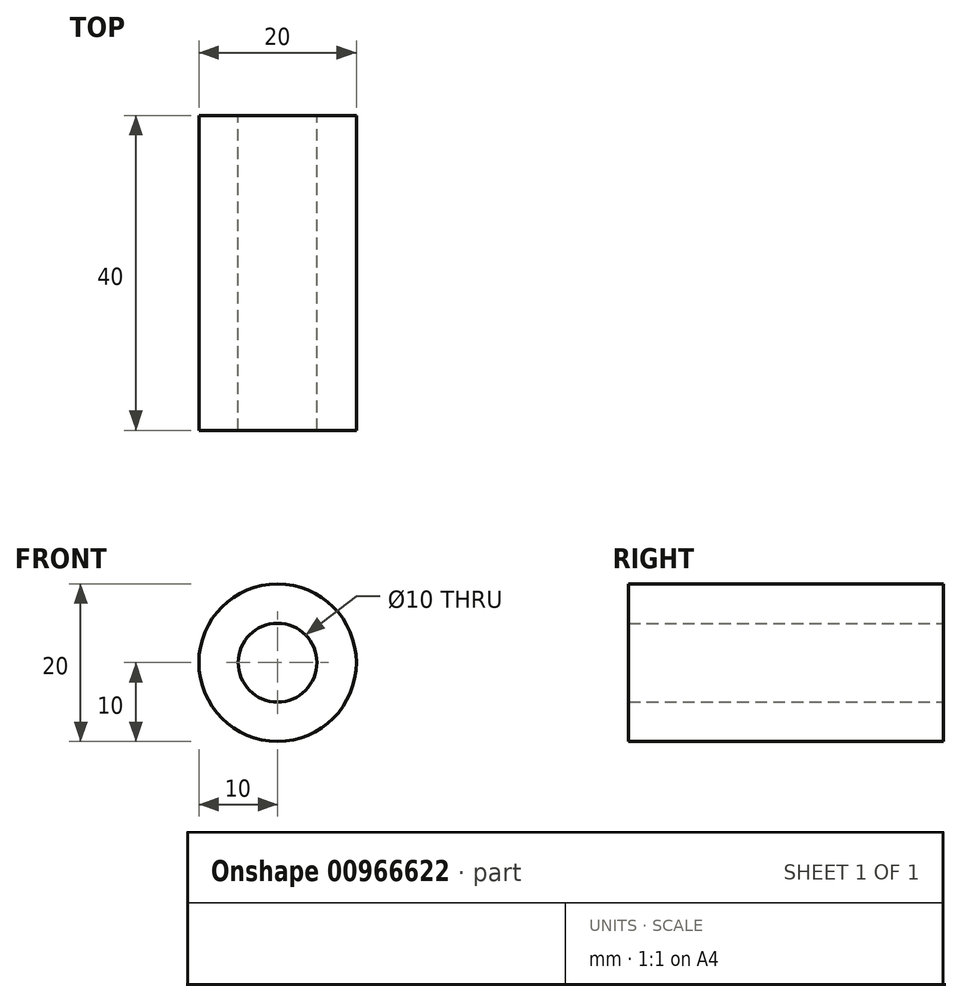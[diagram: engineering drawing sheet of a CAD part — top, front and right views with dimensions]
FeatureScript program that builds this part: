
annotation { "Feature Type Name" : "Feature", "Feature Type Description" : "" }
export const myFeature = defineFeature(function(context is Context, id is Id, definition is map)
    precondition{}
    {
        {
            var Q0;
            Q0=qCreatedBy(makeId("Front.planeOp"),FACE);
            var sketch = newSketch(context, id + "F0", { "sketchPlane" : qUnion([Q0])});
            skCircle(sketch, "E0", {"center": v(0, 0) * mm, "radius": 10 * mm});
            skCircle(sketch, "E1", {"center": v(0, 0) * mm, "radius": 5 * mm});
            skSolve(sketch);
        }
        {
            var Q0;
            Q0 = qSketchRegion(id + "F0", true);
            extrude(context, id + "F1", {"entities" : qUnion([Q0]), "depth" : 40 * mm, "offsetDistance" : 25.4 * mm});
        }
    });
